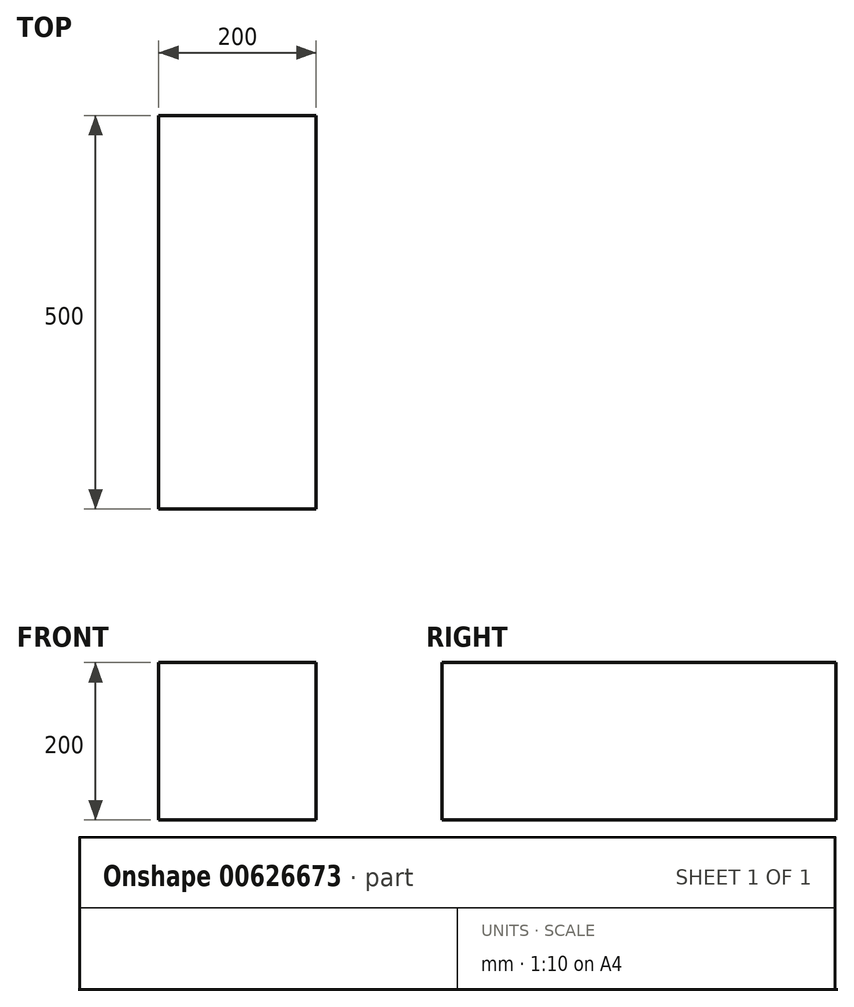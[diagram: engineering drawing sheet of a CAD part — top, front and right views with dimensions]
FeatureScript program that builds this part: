
annotation { "Feature Type Name" : "Feature", "Feature Type Description" : "" }
export const myFeature = defineFeature(function(context is Context, id is Id, definition is map)
    precondition{}
    {
        {
            var Q0;
            Q0=qCreatedBy(makeId("Front.planeOp"),FACE);
            var sketch = newSketch(context, id + "F0", { "sketchPlane" : qUnion([Q0])});
            skArc(sketch, "E0", {"start": v(0, 50) * mm, "mid": v(35.36, 35.36) * mm, "end": v(50, 0) * mm});
            skLineSegment(sketch, "E1", {"start": v(0, 50) * mm, "end": v(0, -50) * mm, "construction": true});
            skSolve(sketch);
        }
        {
            var Q0;
            Q0=sQuery(id+"F0.wireOp",EDGE,"E0");
            var Q1;
            Q1=sQuery(id+"F0.wireOp",EDGE,"E1");
            revolve(context, id + "F1", {"bodyType" : ToolBodyType.SURFACE, "surfaceEntities" : qUnion([Q0]), "axis" : qUnion([Q1]), "revolveType" : RevolveType.ONE_DIRECTION, "angle" : 90 * degree});
        }
        {
            var Q0;
            Q0=makeQuery(id+"F1.opRevolve","SWEPT_BODY",BODY,{"disambiguationData":[OSD([sQuery(id+"F0.wireOp",EDGE,"E0")])]});
            var Q1;
            Q1=qCreatedBy(makeId("Right.planeOp"),FACE);
            mirror(context, id + "F2", {"entities" : qUnion([Q0]), "mirrorPlane" : qUnion([Q1])});
        }
        {
            var Q0;
            Q0=makeQuery(id+"F2.opPattern","COPY",BODY,{"derivedFrom":makeQuery(id+"F1.opRevolve","SWEPT_BODY",BODY,{"disambiguationData":[OSD([sQuery(id+"F0.wireOp",EDGE,"E0")])]}),"instanceName":"1"});
            var Q1;
            Q1=makeQuery(id+"F1.opRevolve","SWEPT_BODY",BODY,{"disambiguationData":[OSD([sQuery(id+"F0.wireOp",EDGE,"E0")])]});
            var Q2;
            Q2=qCreatedBy(makeId("Front.planeOp"),FACE);
            mirror(context, id + "F3", {"entities" : qUnion([Q0, Q1]), "mirrorPlane" : qUnion([Q2])});
        }
        {
            var Q0;
            Q0=makeQuery(id+"F2.opPattern","COPY",BODY,{"derivedFrom":makeQuery(id+"F1.opRevolve","SWEPT_BODY",BODY,{"disambiguationData":[OSD([sQuery(id+"F0.wireOp",EDGE,"E0")])]}),"instanceName":"1"});
            var Q1;
            Q1=makeQuery(id+"F1.opRevolve","SWEPT_BODY",BODY,{"disambiguationData":[OSD([sQuery(id+"F0.wireOp",EDGE,"E0")])]});
            var Q2;
            Q2=makeQuery(id+"F3.opPattern","COPY",BODY,{"derivedFrom":makeQuery(id+"F1.opRevolve","SWEPT_BODY",BODY,{"disambiguationData":[OSD([sQuery(id+"F0.wireOp",EDGE,"E0")])]}),"instanceName":"1"});
            var Q3;
            Q3=makeQuery(id+"F3.opPattern","COPY",BODY,{"derivedFrom":makeQuery(id+"F2.opPattern","COPY",BODY,{"derivedFrom":makeQuery(id+"F1.opRevolve","SWEPT_BODY",BODY,{"disambiguationData":[OSD([sQuery(id+"F0.wireOp",EDGE,"E0")])]}),"instanceName":"1"}),"instanceName":"1"});
            var Q4;
            Q4=qCreatedBy(makeId("Top.planeOp"),FACE);
            mirror(context, id + "F4", {"entities" : qUnion([Q0, Q1, Q2, Q3]), "mirrorPlane" : qUnion([Q4])});
        }
        {
            var Q0;
            Q0=qCreatedBy(makeId("Top.planeOp"),FACE);
            var sketch = newSketch(context, id + "F5", { "sketchPlane" : qUnion([Q0])});
            skLineSegment(sketch, "E2.bottom", {"start": v(100, 250) * mm, "end": v(-100, 250) * mm});
            skLineSegment(sketch, "E2.top", {"start": v(100, -250) * mm, "end": v(-100, -250) * mm});
            skLineSegment(sketch, "E2.left", {"start": v(100, 250) * mm, "end": v(100, -250) * mm});
            skLineSegment(sketch, "E2.right", {"start": v(-100, 250) * mm, "end": v(-100, -250) * mm});
            skPoint(sketch, "E2.middle", {"position": v(0, 0) * mm});
            skSolve(sketch);
        }
        {
            var Q0;
            Q0 = qSketchRegion(id + "F5", true);
            var Q1;
            Q1=sQuery(id+"F5.wireOp",EDGE,"E2.top");
            var Q2;
            Q2=sQuery(id+"F5.wireOp",EDGE,"E2.right");
            var Q3;
            Q3=sQuery(id+"F5.wireOp",EDGE,"E2.left");
            var Q4;
            Q4=sQuery(id+"F5.wireOp",EDGE,"E2.bottom");
            extrude(context, id + "F6", {"entities" : qUnion([Q0]), "surfaceEntities" : qUnion([Q1, Q2, Q3, Q4]), "depth" : 100 * mm, "offsetDistance" : 25 * mm, "hasSecondDirection" : true, "secondDirectionOppositeDirection" : true, "secondDirectionDepth" : 100 * mm});
        }
    });
